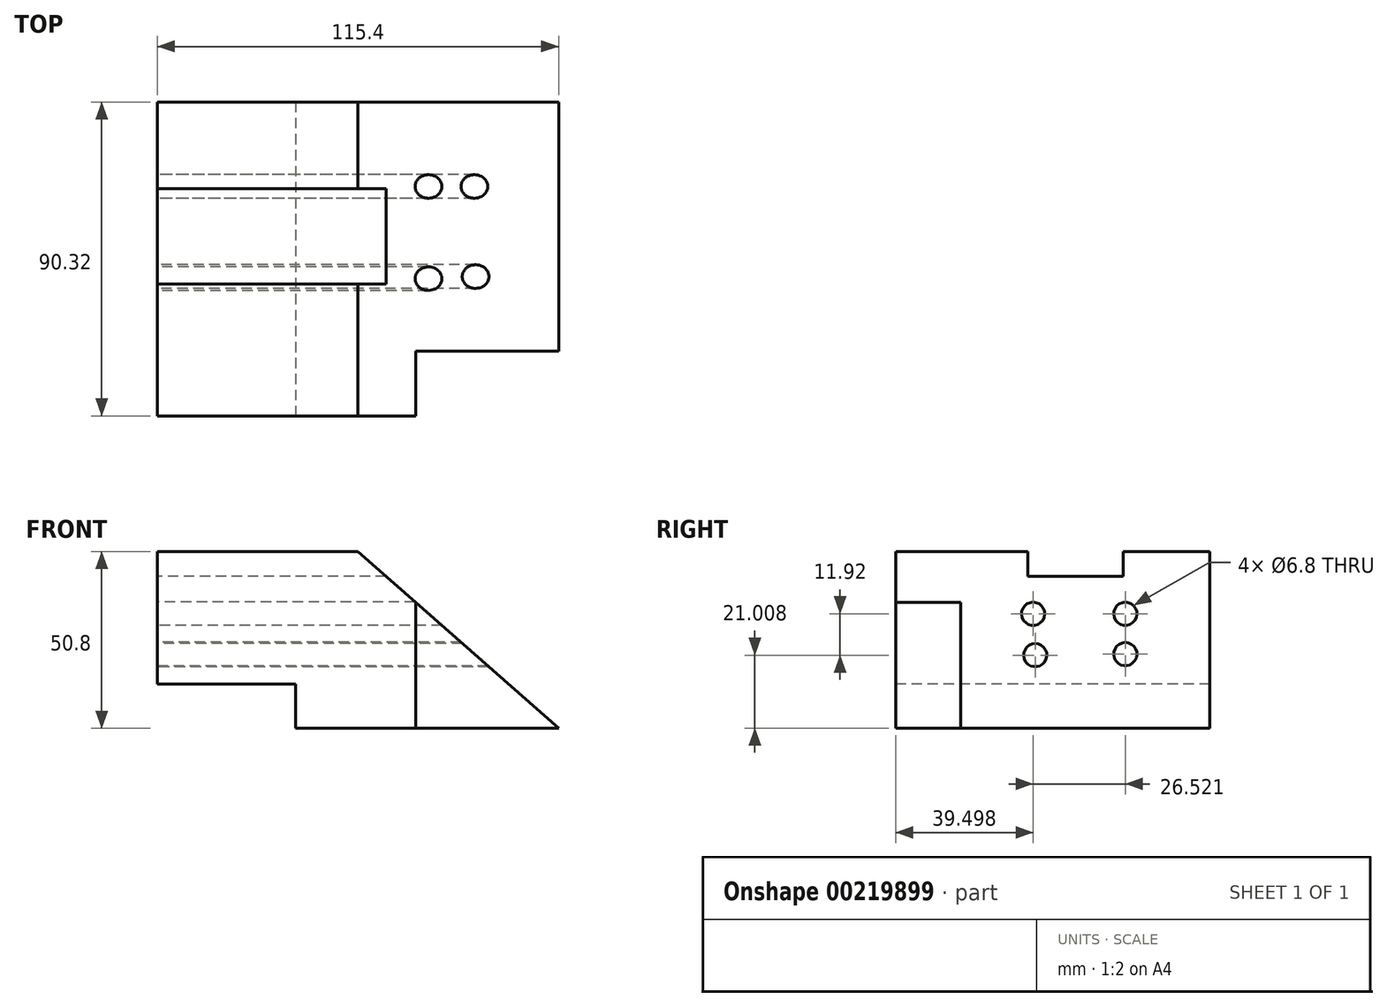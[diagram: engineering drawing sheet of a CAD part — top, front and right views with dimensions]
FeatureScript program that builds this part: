
annotation { "Feature Type Name" : "Feature", "Feature Type Description" : "" }
export const myFeature = defineFeature(function(context is Context, id is Id, definition is map)
    precondition{}
    {
        {
            var Q0;
            Q0=qCreatedBy(makeId("Top.planeOp"),FACE);
            var sketch = newSketch(context, id + "F0", { "sketchPlane" : qUnion([Q0])});
            skLineSegment(sketch, "E0.bottom", {"start": v(-57.7, 45.16) * mm, "end": v(57.7, 45.16) * mm});
            skLineSegment(sketch, "E0.top", {"start": v(-57.7, -45.16) * mm, "end": v(57.7, -45.16) * mm});
            skLineSegment(sketch, "E0.left", {"start": v(-57.7, 45.16) * mm, "end": v(-57.7, -45.16) * mm});
            skLineSegment(sketch, "E0.right", {"start": v(57.7, 45.16) * mm, "end": v(57.7, -45.16) * mm});
            skPoint(sketch, "E0.middle", {"position": v(0, 0) * mm});
            skSolve(sketch);
        }
        {
            var Q0;
            Q0 = qSketchRegion(id + "F0", true);
            extrude(context, id + "F1", {"entities" : qUnion([Q0]), "depth" : 50.8 * mm});
        }
        {
            var Q0;
            Q0=makeQuery(id+"F1.opExtrude","SWEPT_FACE",FACE,{"disambiguationData":[OSD([sQuery(id+"F0.wireOp",EDGE,"E0.top")])]});
            var sketch = newSketch(context, id + "F2", { "sketchPlane" : qUnion([Q0])});
            skLineSegment(sketch, "E1", {"start": v(0, 50.8) * mm, "end": v(57.7, 0) * mm});
            skLineSegment(sketch, "E2", {"start": v(57.7, 50.8) * mm, "end": v(0, 50.8) * mm});
            skLineSegment(sketch, "E3.bottom", {"start": v(-57.7, 0) * mm, "end": v(-17.94, 0) * mm});
            skLineSegment(sketch, "E3.top", {"start": v(-57.7, 12.65) * mm, "end": v(-17.94, 12.65) * mm});
            skLineSegment(sketch, "E3.left", {"start": v(-57.7, 0) * mm, "end": v(-57.7, 12.65) * mm});
            skLineSegment(sketch, "E3.right", {"start": v(-17.94, 0) * mm, "end": v(-17.94, 12.65) * mm});
            skSolve(sketch);
        }
        {
            var Q0;
            Q0=makeQuery(id+"F2.imprint","IMPRINT",FACE,{"disambiguationData":[TD([[makeQuery(id+"F2.imprint","IMPRINT",EDGE,{"derivedFrom":sQuery(id+"F2.wireOp",EDGE,"E1")}),1.0]])]});
            var Q1;
            Q1=makeQuery(id+"F2.imprint","IMPRINT",FACE,{"disambiguationData":[TD([[makeQuery(id+"F2.imprint","IMPRINT",EDGE,{"derivedFrom":sQuery(id+"F2.wireOp",EDGE,"E3.bottom")}),1.0]])]});
            extrude(context, id + "F3", {"entities" : qUnion([Q0, Q1]), "operationType" : NewBodyOperationType.REMOVE, "endBound" : BoundingType.THROUGH_ALL, "oppositeDirection" : true, "depth" : 25.4 * mm});
        }
        {
            var Q0;
            Q0=makeQuery(id+"F1.opExtrude","CAP_FACE",FACE,{"disambiguationData":[OSD([sQuery(id+"F0.wireOp",EDGE,"E0.bottom"),sQuery(id+"F0.wireOp",EDGE,"E0.top"),sQuery(id+"F0.wireOp",EDGE,"E0.left"),sQuery(id+"F0.wireOp",EDGE,"E0.right")])],"isStart":true});
            var sketch = newSketch(context, id + "F4", { "sketchPlane" : qUnion([Q0])});
            skLineSegment(sketch, "E4.bottom", {"start": v(57.7, 45.16) * mm, "end": v(16.6, 45.16) * mm});
            skLineSegment(sketch, "E4.top", {"start": v(57.7, 26.53) * mm, "end": v(16.6, 26.53) * mm});
            skLineSegment(sketch, "E4.left", {"start": v(57.7, 45.16) * mm, "end": v(57.7, 26.53) * mm});
            skLineSegment(sketch, "E4.right", {"start": v(16.6, 45.16) * mm, "end": v(16.6, 26.53) * mm});
            skSolve(sketch);
        }
        {
            var Q0;
            Q0=makeQuery(id+"F4.imprint","IMPRINT",FACE,{"disambiguationData":[TD([[makeQuery(id+"F4.imprint","IMPRINT",EDGE,{"derivedFrom":sQuery(id+"F4.wireOp",EDGE,"E4.bottom")}),-1.0]])]});
            extrude(context, id + "F5", {"entities" : qUnion([Q0]), "operationType" : NewBodyOperationType.REMOVE, "endBound" : BoundingType.THROUGH_ALL, "oppositeDirection" : true, "depth" : 25.4 * mm});
        }
        {
            var Q0;
            Q0=makeQuery(id+"F1.opExtrude","SWEPT_FACE",FACE,{"disambiguationData":[OSD([sQuery(id+"F0.wireOp",EDGE,"E0.left")])]});
            var sketch = newSketch(context, id + "F6", { "sketchPlane" : qUnion([Q0])});
            skLineSegment(sketch, "E5.bottom", {"start": v(-20.26, 50.8) * mm, "end": v(7.15, 50.8) * mm});
            skLineSegment(sketch, "E5.top", {"start": v(-20.26, 43.66) * mm, "end": v(7.15, 43.66) * mm});
            skLineSegment(sketch, "E5.left", {"start": v(-20.26, 50.8) * mm, "end": v(-20.26, 43.66) * mm});
            skLineSegment(sketch, "E5.right", {"start": v(7.15, 50.8) * mm, "end": v(7.15, 43.66) * mm});
            skPoint(sketch, "E5.middle", {"position": v(-6.56, 47.23) * mm});
            skCircle(sketch, "E6", {"center": v(-20.86, 32.93) * mm, "radius": 3.4 * mm});
            skCircle(sketch, "E7", {"center": v(5.66, 32.93) * mm, "radius": 3.4 * mm});
            skCircle(sketch, "E8", {"center": v(5.07, 21) * mm, "radius": 3.4 * mm});
            skCircle(sketch, "E9", {"center": v(-20.86, 21.3) * mm, "radius": 3.4 * mm});
            skPoint(sketch, "E10.orphan", {"position": v(-6.56, 32.93) * mm});
            skSolve(sketch);
        }
        {
            var Q0;
            Q0=makeQuery(id+"F6.imprint","IMPRINT",FACE,{"disambiguationData":[TD([[makeQuery(id+"F6.imprint","IMPRINT",EDGE,{"derivedFrom":sQuery(id+"F6.wireOp",EDGE,"E9")}),1.0]])]});
            var Q1;
            Q1=makeQuery(id+"F6.imprint","IMPRINT",FACE,{"disambiguationData":[TD([[makeQuery(id+"F6.imprint","IMPRINT",EDGE,{"derivedFrom":sQuery(id+"F6.wireOp",EDGE,"E6")}),1.0]])]});
            var Q2;
            Q2=makeQuery(id+"F6.imprint","IMPRINT",FACE,{"disambiguationData":[TD([[makeQuery(id+"F6.imprint","IMPRINT",EDGE,{"derivedFrom":sQuery(id+"F6.wireOp",EDGE,"E7")}),1.0]])]});
            var Q3;
            Q3=makeQuery(id+"F6.imprint","IMPRINT",FACE,{"disambiguationData":[TD([[makeQuery(id+"F6.imprint","IMPRINT",EDGE,{"derivedFrom":sQuery(id+"F6.wireOp",EDGE,"E8")}),1.0]])]});
            var Q4;
            Q4=makeQuery(id+"F6.imprint","IMPRINT",FACE,{"disambiguationData":[TD([[makeQuery(id+"F6.imprint","IMPRINT",EDGE,{"derivedFrom":sQuery(id+"F6.wireOp",EDGE,"E5.bottom")}),-1.0]])]});
            extrude(context, id + "F7", {"entities" : qUnion([Q0, Q1, Q2, Q3, Q4]), "operationType" : NewBodyOperationType.REMOVE, "endBound" : BoundingType.THROUGH_ALL, "oppositeDirection" : true, "depth" : 25.4 * mm});
        }
    });
